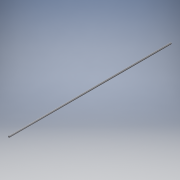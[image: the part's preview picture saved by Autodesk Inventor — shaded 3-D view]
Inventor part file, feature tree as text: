
AUTODESK INVENTOR PART (.ipt)
format: ipt  version: 2016 (Build 200138000, 138)  size: 98,816 bytes
history: native  units: mm
features: extrude x1, chamfer x1, sketch x1
ambient origin geometry x8: Origin, YZ Plane, XZ Plane, XY Plane, X Axis, Y Axis, Z Axis, Center Point
bodies: Solid1 (feature_tree)
feature tree (3):
  extrude  "Extrusion1"  Depth=304.8mm TaperAngle=0.0deg
  chamfer  "Chamfer1"  Distance=0.2mm Angle=45.0deg
  sketch  "Sketch2"  dims[d5=3.0mm d6=304.8mm d7=0.0mm d8=0.2mm d9=2.0mm d10=45.0deg]
